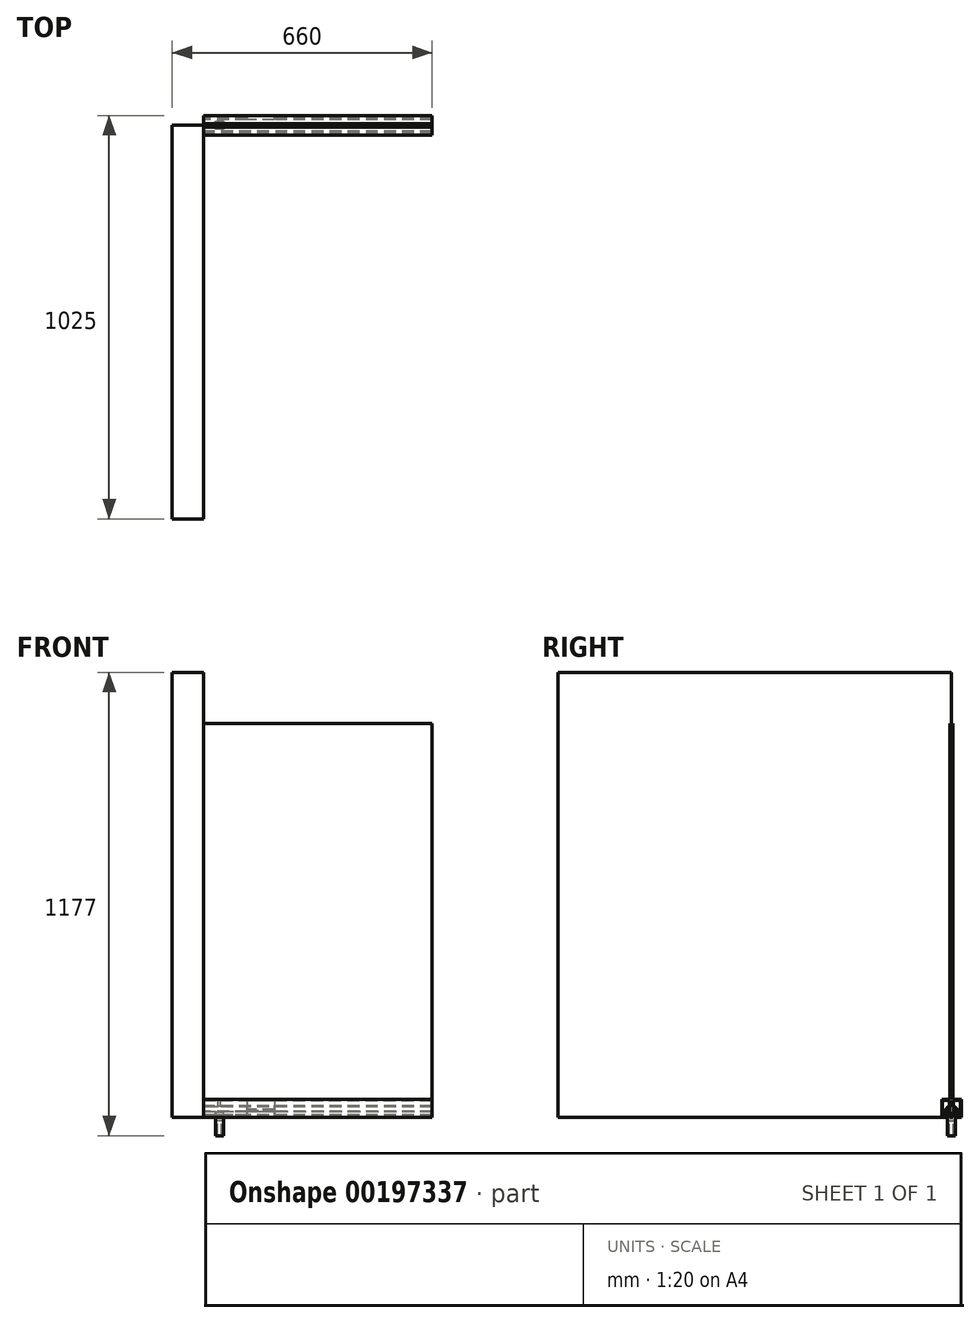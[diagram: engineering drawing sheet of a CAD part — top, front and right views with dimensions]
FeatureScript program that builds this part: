
annotation { "Feature Type Name" : "Feature", "Feature Type Description" : "" }
export const myFeature = defineFeature(function(context is Context, id is Id, definition is map)
    precondition{}
    {
        {
            var Q0;
            Q0=qCreatedBy(makeId("Right.planeOp"),FACE);
            var sketch = newSketch(context, id + "F0", { "sketchPlane" : qUnion([Q0])});
            skLineSegment(sketch, "E0", {"start": v(-25, 45) * mm, "end": v(25, 45) * mm});
            skLineSegment(sketch, "E1", {"start": v(25, 45) * mm, "end": v(25, 0) * mm});
            skLineSegment(sketch, "E2", {"start": v(25, 0) * mm, "end": v(15, 0) * mm});
            skLineSegment(sketch, "E3", {"start": v(15, 0) * mm, "end": v(15, 2) * mm});
            skLineSegment(sketch, "E4", {"start": v(15, 2) * mm, "end": v(23, 2) * mm});
            skLineSegment(sketch, "E5", {"start": v(23, 2) * mm, "end": v(23, 43) * mm});
            skLineSegment(sketch, "E6", {"start": v(23, 43) * mm, "end": v(-23, 43) * mm});
            skLineSegment(sketch, "E7", {"start": v(-23, 43) * mm, "end": v(-23, 2) * mm});
            skLineSegment(sketch, "E8", {"start": v(-23, 2) * mm, "end": v(-15, 2) * mm});
            skLineSegment(sketch, "E9", {"start": v(-15, 2) * mm, "end": v(-15, 0) * mm});
            skLineSegment(sketch, "E10", {"start": v(-15, 0) * mm, "end": v(-25, 0) * mm});
            skLineSegment(sketch, "E11", {"start": v(-25, 0) * mm, "end": v(-25, 45) * mm});
            skSolve(sketch);
        }
        {
            var Q0;
            Q0=qCreatedBy(makeId("Right.planeOp"),FACE);
            var sketch = newSketch(context, id + "F1", { "sketchPlane" : qUnion([Q0])});
            skLineSegment(sketch, "E12", {"start": v(-21.5, 0) * mm, "end": v(-25, 0) * mm});
            skLineSegment(sketch, "E13", {"start": v(-25, 0) * mm, "end": v(-25, 15) * mm});
            skLineSegment(sketch, "E14", {"start": v(-25, 15) * mm, "end": v(-20, 15) * mm});
            skLineSegment(sketch, "E15", {"start": v(25, 15) * mm, "end": v(25, 0) * mm});
            skLineSegment(sketch, "E16", {"start": v(25, 0) * mm, "end": v(21.5, 0) * mm});
            skLineSegment(sketch, "E17", {"start": v(21.5, 0) * mm, "end": v(21.5, 2) * mm});
            skLineSegment(sketch, "E18", {"start": v(21.5, 2) * mm, "end": v(23, 2) * mm});
            skLineSegment(sketch, "E19", {"start": v(23, 2) * mm, "end": v(23, 4) * mm});
            skLineSegment(sketch, "E20", {"start": v(23, 4) * mm, "end": v(17, 4) * mm});
            skLineSegment(sketch, "E21", {"start": v(17, 4) * mm, "end": v(17, 2) * mm});
            skLineSegment(sketch, "E22", {"start": v(17, 2) * mm, "end": v(18.5, 2) * mm});
            skLineSegment(sketch, "E23", {"start": v(18.5, 2) * mm, "end": v(18.5, 0) * mm});
            skLineSegment(sketch, "E24", {"start": v(18.5, 0) * mm, "end": v(15, 0) * mm});
            skLineSegment(sketch, "E25", {"start": v(-15, 6) * mm, "end": v(-15, 0) * mm});
            skLineSegment(sketch, "E26", {"start": v(-15, 0) * mm, "end": v(-18.5, 0) * mm});
            skLineSegment(sketch, "E27", {"start": v(-18.5, 0) * mm, "end": v(-18.5, 2) * mm});
            skLineSegment(sketch, "E28", {"start": v(-18.5, 2) * mm, "end": v(-17, 2) * mm});
            skLineSegment(sketch, "E29", {"start": v(-17, 2) * mm, "end": v(-17, 4) * mm});
            skLineSegment(sketch, "E30", {"start": v(-17, 4) * mm, "end": v(-23, 4) * mm});
            skLineSegment(sketch, "E31", {"start": v(-23, 4) * mm, "end": v(-23, 2) * mm});
            skLineSegment(sketch, "E32", {"start": v(-23, 2) * mm, "end": v(-21.5, 2) * mm});
            skLineSegment(sketch, "E33", {"start": v(-21.5, 2) * mm, "end": v(-21.5, 0) * mm});
            skLineSegment(sketch, "E34", {"start": v(-15, 6) * mm, "end": v(-23, 6) * mm});
            skLineSegment(sketch, "E35", {"start": v(-23, 6) * mm, "end": v(-23, 13) * mm});
            skLineSegment(sketch, "E36", {"start": v(-23, 13) * mm, "end": v(23, 13) * mm});
            skLineSegment(sketch, "E37", {"start": v(23, 13) * mm, "end": v(23, 6) * mm});
            skLineSegment(sketch, "E38", {"start": v(23, 6) * mm, "end": v(15, 6) * mm});
            skLineSegment(sketch, "E39", {"start": v(15, 6) * mm, "end": v(15, 0) * mm});
            skLineSegment(sketch, "E40", {"start": v(-20, 15) * mm, "end": v(-7.41, 27.59) * mm});
            skLineSegment(sketch, "E41", {"start": v(-4, 26.17) * mm, "end": v(-4, 15) * mm});
            skLineSegment(sketch, "E42", {"start": v(-4, 15) * mm, "end": v(4, 15) * mm});
            skLineSegment(sketch, "E43", {"start": v(4, 15) * mm, "end": v(4, 26.17) * mm});
            skLineSegment(sketch, "E44", {"start": v(7.41, 27.59) * mm, "end": v(20, 15) * mm});
            skLineSegment(sketch, "E45", {"start": v(-17.17, 15) * mm, "end": v(-6, 26.17) * mm});
            skLineSegment(sketch, "E46", {"start": v(-6, 26.17) * mm, "end": v(-6, 15) * mm});
            skLineSegment(sketch, "E47", {"start": v(17.17, 15) * mm, "end": v(6, 26.17) * mm});
            skLineSegment(sketch, "E48", {"start": v(6, 26.17) * mm, "end": v(6, 15) * mm});
            skLineSegment(sketch, "E49.trimOffspring", {"start": v(-17.17, 15) * mm, "end": v(-6, 15) * mm});
            skLineSegment(sketch, "E50.trimOffspring", {"start": v(20, 15) * mm, "end": v(25, 15) * mm});
            skLineSegment(sketch, "E51.trimOffspring", {"start": v(6, 15) * mm, "end": v(17.17, 15) * mm});
            skLineSegment(sketch, "E52", {"start": v(-20, 6) * mm, "end": v(-20, 0) * mm, "construction": true});
            skPoint(sketch, "E53.visualSharp", {"position": v(-4, 31) * mm});
            skArc(sketch, "E53.filletArc", {"start": v(-4, 26.17) * mm, "mid": v(-5.23, 28.02) * mm, "end": v(-7.41, 27.59) * mm});
            skPoint(sketch, "E54.visualSharp", {"position": v(4, 31) * mm});
            skArc(sketch, "E54.filletArc", {"start": v(7.41, 27.59) * mm, "mid": v(5.23, 28.02) * mm, "end": v(4, 26.17) * mm});
            skSolve(sketch);
        }
        {
            var Q0;
            Q0=qCreatedBy(makeId("Right.planeOp"),FACE);
            var sketch = newSketch(context, id + "F2", { "sketchPlane" : qUnion([Q0])});
            skLineSegment(sketch, "E55.bottom", {"start": v(-4, 1000) * mm, "end": v(4, 1000) * mm});
            skLineSegment(sketch, "E55.top", {"start": v(-4, 0) * mm, "end": v(4, 0) * mm});
            skLineSegment(sketch, "E55.left", {"start": v(-4, 1000) * mm, "end": v(-4, 0) * mm});
            skLineSegment(sketch, "E55.right", {"start": v(4, 1000) * mm, "end": v(4, 0) * mm});
            skSolve(sketch);
        }
        {
            var Q0;
            Q0 = qSketchRegion(id + "F0", true);
            extrude(context, id + "F3", {"entities" : qUnion([Q0]), "depth" : 580 * mm});
        }
        {
            var Q0;
            Q0 = qSketchRegion(id + "F1", true);
            extrude(context, id + "F4", {"entities" : qUnion([Q0]), "depth" : 580 * mm});
        }
        {
            var Q0;
            Q0 = qSketchRegion(id + "F2", true);
            extrude(context, id + "F5", {"entities" : qUnion([Q0]), "depth" : 580 * mm});
        }
        {
            var Q0;
            Q0=makeQuery(id+"F3.opExtrude","SWEPT_FACE",FACE,{"disambiguationData":[OSD([sQuery(id+"F0.wireOp",EDGE,"E0")])]});
            var sketch = newSketch(context, id + "F6", { "sketchPlane" : qUnion([Q0])});
            skCircle(sketch, "E56", {"center": v(40, 0) * mm, "radius": 5 * mm});
            skSolve(sketch);
        }
        {
            var Q0;
            Q0 = qSketchRegion(id + "F6", true);
            extrude(context, id + "F7", {"entities" : qUnion([Q0]), "operationType" : NewBodyOperationType.ADD, "oppositeDirection" : true, "depth" : 55 * mm});
        }
        {
            var Q0;
            Q0=makeQuery(id+"F4.opExtrude","SWEPT_FACE",FACE,{"disambiguationData":[OSD([sQuery(id+"F1.wireOp",EDGE,"E36")])]});
            var sketch = newSketch(context, id + "F8", { "sketchPlane" : qUnion([Q0])});
            skCircle(sketch, "E57", {"center": v(40, 0) * mm, "radius": 5 * mm});
            skPoint(sketch, "E57.centerSnap0", {"position": v(0, 0) * mm});
            skLineSegment(sketch, "E58", {"start": v(30, 10) * mm, "end": v(30, -10) * mm});
            skLineSegment(sketch, "E59", {"start": v(30, -10) * mm, "end": v(50, -10) * mm});
            skLineSegment(sketch, "E60", {"start": v(50, -10) * mm, "end": v(50, 10) * mm});
            skLineSegment(sketch, "E61", {"start": v(50, 10) * mm, "end": v(30, 10) * mm});
            skSolve(sketch);
        }
        {
            var Q0;
            Q0 = qSketchRegion(id + "F8", true);
            extrude(context, id + "F9", {"entities" : qUnion([Q0]), "operationType" : NewBodyOperationType.ADD, "depth" : 60 * mm});
        }
        {
            var Q0;
            Q0=qCreatedBy(makeId("Front.planeOp"),FACE);
            var sketch = newSketch(context, id + "F10", { "sketchPlane" : qUnion([Q0])});
            skLineSegment(sketch, "E62.bottom", {"start": v(0, 1130) * mm, "end": v(-80, 1130) * mm});
            skLineSegment(sketch, "E62.top", {"start": v(0, 0) * mm, "end": v(-80, 0) * mm});
            skLineSegment(sketch, "E62.left", {"start": v(0, 1130) * mm, "end": v(0, 0) * mm});
            skLineSegment(sketch, "E62.right", {"start": v(-80, 1130) * mm, "end": v(-80, 0) * mm});
            skSolve(sketch);
        }
        {
            var Q0;
            Q0 = qSketchRegion(id + "F10", true);
            extrude(context, id + "F11", {"entities" : qUnion([Q0]), "depth" : 1000 * mm});
        }
        {
            var Q0;
            Q0 = qSketchRegion(id + "F0", true);
            extrude(context, id + "F12", {"entities" : qUnion([Q0]), "depth" : 580 * mm});
        }
        {
            var Q0;
            Q0=makeQuery(id+"F12.opExtrude","SWEPT_FACE",FACE,{"disambiguationData":[OSD([sQuery(id+"F0.wireOp",EDGE,"E1")])]});
            var sketch = newSketch(context, id + "F13", { "sketchPlane" : qUnion([Q0])});
            skLineSegment(sketch, "E63.bottom", {"start": v(-110, 0) * mm, "end": v(-180, 0) * mm});
            skLineSegment(sketch, "E63.top", {"start": v(-110, 42) * mm, "end": v(-180, 42) * mm});
            skLineSegment(sketch, "E63.left", {"start": v(-110, 0) * mm, "end": v(-110, 42) * mm});
            skLineSegment(sketch, "E63.right", {"start": v(-180, 0) * mm, "end": v(-180, 42) * mm});
            skSolve(sketch);
        }
        {
            var Q0;
            Q0 = qSketchRegion(id + "F13", true);
            extrude(context, id + "F14", {"entities" : qUnion([Q0]), "operationType" : NewBodyOperationType.REMOVE, "oppositeDirection" : true, "depth" : 10 * mm});
        }
        {
            var Q0;
            Q0 = qSketchRegion(id + "F6", true);
            extrude(context, id + "F15", {"entities" : qUnion([Q0]), "operationType" : NewBodyOperationType.ADD, "oppositeDirection" : true, "depth" : 55 * mm});
        }
    });
